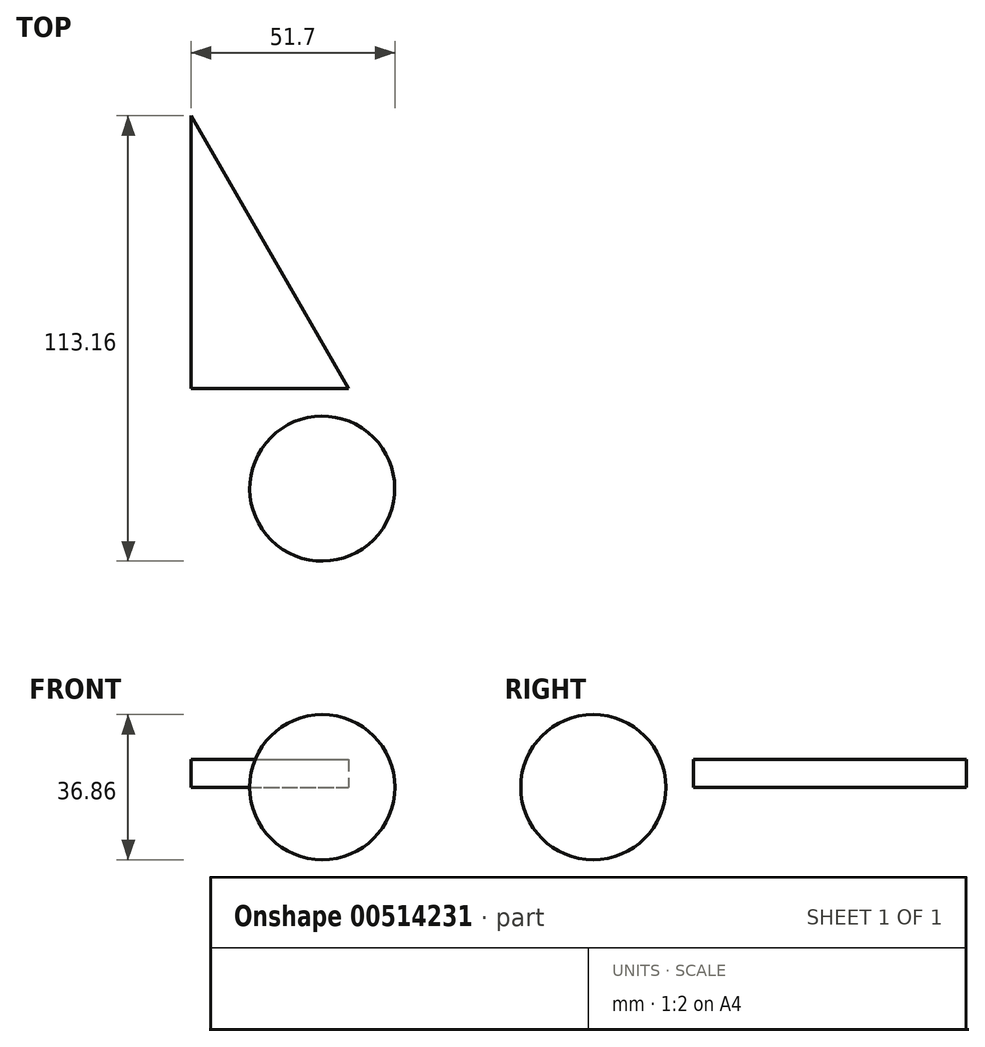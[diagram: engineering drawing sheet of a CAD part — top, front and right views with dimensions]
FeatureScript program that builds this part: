
annotation { "Feature Type Name" : "Feature", "Feature Type Description" : "" }
export const myFeature = defineFeature(function(context is Context, id is Id, definition is map)
    precondition{}
    {
        {
            var Q0;
            Q0=qCreatedBy(makeId("Top.planeOp"),FACE);
            var sketch = newSketch(context, id + "F0", { "sketchPlane" : qUnion([Q0])});
            skLineSegment(sketch, "E0.top", {"start": v(-40, 0) * mm, "end": v(0, 0) * mm});
            skLineSegment(sketch, "E0.left", {"start": v(-40, 69.28) * mm, "end": v(-40, 0) * mm});
            skLineSegment(sketch, "E1", {"start": v(-40, 69.28) * mm, "end": v(0, 0) * mm});
            skSolve(sketch);
        }
        {
            var Q0;
            Q0 = qSketchRegion(id + "F0", true);
            extrude(context, id + "F1", {"entities" : qUnion([Q0]), "depth" : 7 * mm});
        }
        {
            var Q0;
            Q0=qCreatedBy(makeId("Top.planeOp"),FACE);
            var sketch = newSketch(context, id + "F2", { "sketchPlane" : qUnion([Q0])});
            skLineSegment(sketch, "E2", {"start": v(-16.85, -40.85) * mm, "end": v(-6.73, -25.45) * mm, "construction": true});
            skLineSegment(sketch, "E3", {"start": v(-6.73, -25.45) * mm, "end": v(3.39, -10.05) * mm, "construction": true});
            skLineSegment(sketch, "E4", {"start": v(-16.85, -40.85) * mm, "end": v(3.39, -10.05) * mm});
            skArc(sketch, "E5", {"start": v(-16.85, -40.85) * mm, "mid": v(-22.13, -15.33) * mm, "end": v(3.39, -10.05) * mm});
            skSolve(sketch);
        }
        {
            var Q0;
            Q0 = qSketchRegion(id + "F2", true);
            var Q1;
            Q1=sQuery(id+"F2.wireOp",EDGE,"E4");
            revolve(context, id + "F3", {"entities" : qUnion([Q0]), "axis" : qUnion([Q1]), "revolveType" : RevolveType.FULL});
        }
    });
